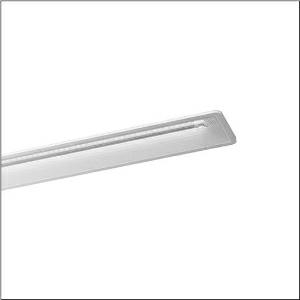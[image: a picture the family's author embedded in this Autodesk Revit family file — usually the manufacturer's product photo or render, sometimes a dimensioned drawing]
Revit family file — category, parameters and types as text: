
# Revit family: taris_r__21_5mt117703wd_45ff
name_source: partatom
category: Lighting Fixtures
units: mm (PartAtom-declared; Revit-internal decimal feet)

## family parameters
Cut with Voids When Loaded = No
Host = Face
Light Source = No
Part Type = Normal
Room Calculation Point = No
Round Connector Dimension = Use Diameter
Shared = No

## types (1)
- Taris® 21 (1 x LED, 5700 lm, 37 W, 3000K)
    Apparent Load = 37 VA
    CIE Flux Codes = 73 96 99 100 100
    Color Rendering = 80
    Color Temperature = 3000K
    Default Elevation = 1800 mm
    Description = Taris® 21, office luminaire, primary anti-glare with micro louvre, primary optical cover: axial lens, of PMMA, structured, CAT 2 (L<= 1500cd/m²), light emission: direct distribution, primary light characteristic: symmetric, installation type: recessed, LED rated luminous flux: 5.700 lm, light colour: 830, colour temperature: 3000K, control gear: ECG, with terminal, 5-pole, mains connection: 230V, AC, 50Hz, rated input power: 37W, housing, luminaire housing, of plastic, pure white, length: 1.530 mm, width: 150 mm, height: 76mm, recess depth: 106 mm, protection rating (complete): IP20, insulation class (complete): insulation class I (protective earthing), certification: CE, ENEC, VDE, protection symbol: F, impact resistance: IK02, permissible ambient temperature for indoor applications: 0..+35°C, standard: EN 50419, packaging unit: 1 piece
    Height = 0 mm  [stored 0 ft]
    Lamp = 1 x LED
    Lamp Light Flux = 5700 lm
    Lamp Power = 37 W
    Lamp count = 1
    Length = 1524 mm  [stored 5 ft]
    Luminous efficacy = 154 lm/W
    Manufacturer = Siteco
    ModVariant = No
    Model = 5MT117703WD
    Mounting Place = Ceiling
    Mounting Type = Recessed
    Number of Poles = 1
    OnlyDefault = Yes
    Power Factor = 1
    Product Name = Taris® 21
    Product group = office luminaire | ceiling recessed
    ProductGroupID = 400
    Protection Class = Protection class I
    Protection Degree = IP 20
    RLX_Detail_Level = 1
    RlxData = <blob elided: 26761 chars, md5=a148bbc7>
    Socket = socket
    Standby Power = 0 W
    System Light Flux = 5700 lm
    System Power = 37 W
    Type Comments = Product without accessories
    Type Image = l_1004723.jpg
    URL = http://relux.com
    VarID = ---
    Voltage = 0 V
    Weight = 0.00 kg
    Width = 144 mm

note: [stored X ft] marks values corroborated as IEEE doubles in the binary element streams (Revit-internal decimal feet)

## geometry (parser evidence)
native form markers: Blend x4, Sweep x11
no freeform markers — native parametric forms only
